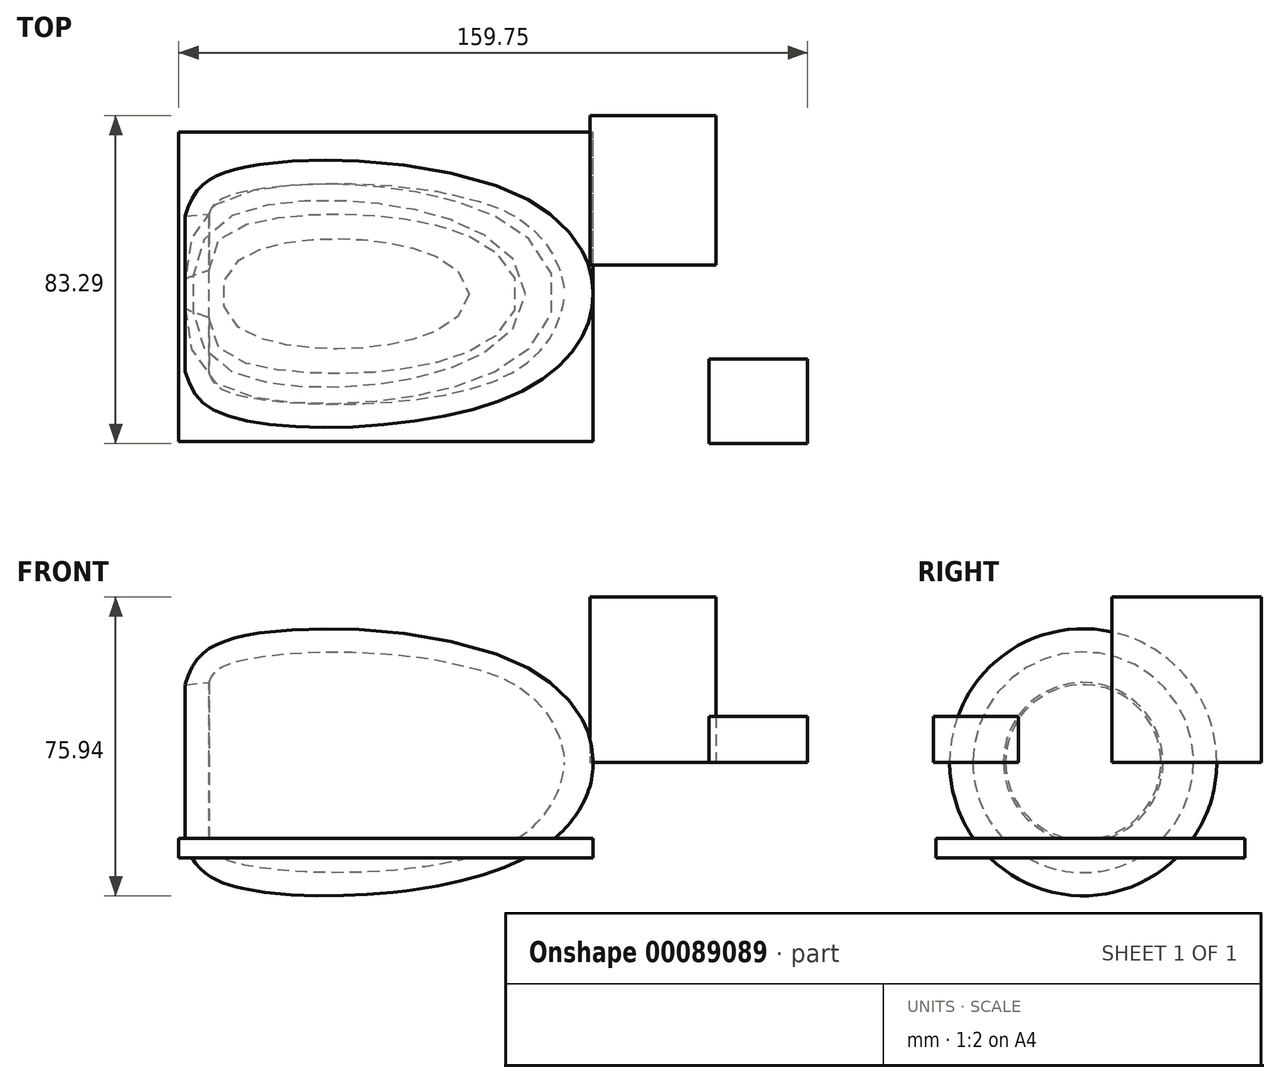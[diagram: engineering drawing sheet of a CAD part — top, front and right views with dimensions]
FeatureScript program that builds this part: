
annotation { "Feature Type Name" : "Feature", "Feature Type Description" : "" }
export const myFeature = defineFeature(function(context is Context, id is Id, definition is map)
    precondition{}
    {
        {
            var Q0;
            Q0=qCreatedBy(makeId("Top.planeOp"),FACE);
            var sketch = newSketch(context, id + "F0", { "sketchPlane" : qUnion([Q0])});
            skFitSpline(sketch, "E0", {"points": [v(0, 0) * mm, v(-17.7, -24.57) * mm, v(-92.32, -31.2) * mm, v(-103.63, -19.71) * mm], "startDerivative": vector(2.43, -78.93) * mm, "endDerivative": vector(-22.13, 76.46) * mm});
            skLineSegment(sketch, "E1", {"start": v(-103.63, -19.71) * mm, "end": v(-97.62, -20.26) * mm});
            skLineSegment(sketch, "E2", {"start": v(0, 0) * mm, "end": v(-7.26, 0) * mm});
            skFitSpline(sketch, "E3", {"points": [v(-97.62, -20.26) * mm, v(-91.53, -25.34) * mm, v(-20.71, -20.17) * mm, v(-7.26, 0) * mm], "startDerivative": vector(12.73, -36.05) * mm, "endDerivative": vector(2.5, 51.01) * mm});
            skSolve(sketch);
        }
        {
            var Q0;
            Q0=qCreatedBy(makeId("Top.planeOp"),FACE);
            var sketch = newSketch(context, id + "F1", { "sketchPlane" : qUnion([Q0])});
            skLineSegment(sketch, "E4", {"start": v(-123.98, 0) * mm, "end": v(-10.9, 0) * mm});
            skSolve(sketch);
        }
        {
            var Q0;
            Q0=makeQuery(id+"F0.imprint","IMPRINT",FACE,{"disambiguationData":[TD([[makeQuery(id+"F0.imprint","IMPRINT",EDGE,{"derivedFrom":sQuery(id+"F0.wireOp",EDGE,"E0")}),-1.0]])]});
            var Q1;
            Q1=sQuery(id+"F1.wireOp",EDGE,"E4");
            revolve(context, id + "F2", {"entities" : qUnion([Q0]), "axis" : qUnion([Q1]), "revolveType" : RevolveType.FULL});
        }
        {
            var Q0;
            Q0=qCreatedBy(makeId("Front.planeOp"),FACE);
            var sketch = newSketch(context, id + "F3", { "sketchPlane" : qUnion([Q0])});
            skLineSegment(sketch, "E5.bottom", {"start": v(-105.25, -19.35) * mm, "end": v(0, -19.35) * mm});
            skLineSegment(sketch, "E5.top", {"start": v(-105.25, -24.3) * mm, "end": v(0, -24.3) * mm});
            skLineSegment(sketch, "E5.left", {"start": v(-105.25, -19.35) * mm, "end": v(-105.25, -24.3) * mm});
            skLineSegment(sketch, "E5.right", {"start": v(0, -19.35) * mm, "end": v(0, -24.3) * mm});
            skSolve(sketch);
        }
        {
            var Q0;
            Q0=makeQuery(id+"F3.imprint","IMPRINT",FACE,{"disambiguationData":[TD([[makeQuery(id+"F3.imprint","IMPRINT",EDGE,{"derivedFrom":sQuery(id+"F3.wireOp",EDGE,"E5.bottom")}),-1.0]])]});
            extrude(context, id + "F4", {"entities" : qUnion([Q0]), "operationType" : NewBodyOperationType.ADD, "depth" : 37.48 * mm, "hasSecondDirection" : true, "secondDirectionOppositeDirection" : true, "secondDirectionDepth" : 41.05 * mm});
        }
        {
            var Q0;
            Q0=qCreatedBy(makeId("Top.planeOp"),FACE);
            var sketch = newSketch(context, id + "F5", { "sketchPlane" : qUnion([Q0])});
            skLineSegment(sketch, "E6.bottom", {"start": v(29.4, -16.52) * mm, "end": v(54.5, -16.52) * mm});
            skLineSegment(sketch, "E6.top", {"start": v(29.4, -38.02) * mm, "end": v(54.5, -38.02) * mm});
            skLineSegment(sketch, "E6.left", {"start": v(29.4, -16.52) * mm, "end": v(29.4, -38.02) * mm});
            skLineSegment(sketch, "E6.right", {"start": v(54.5, -16.52) * mm, "end": v(54.5, -38.02) * mm});
            skSolve(sketch);
        }
        {
            var Q0;
            Q0 = qSketchRegion(id + "F5", true);
            extrude(context, id + "F6", {"entities" : qUnion([Q0]), "depth" : 11.7 * mm});
        }
        {
            var Q0;
            Q0=qCreatedBy(makeId("Top.planeOp"),FACE);
            var sketch = newSketch(context, id + "F7", { "sketchPlane" : qUnion([Q0])});
            skLineSegment(sketch, "E7.bottom", {"start": v(-0.83, 45.27) * mm, "end": v(31.17, 45.27) * mm});
            skLineSegment(sketch, "E7.top", {"start": v(-0.83, 7.27) * mm, "end": v(31.17, 7.27) * mm});
            skLineSegment(sketch, "E7.left", {"start": v(-0.83, 45.27) * mm, "end": v(-0.83, 7.27) * mm});
            skLineSegment(sketch, "E7.right", {"start": v(31.17, 45.27) * mm, "end": v(31.17, 7.27) * mm});
            skSolve(sketch);
        }
        {
            var Q0;
            Q0 = qSketchRegion(id + "F7", true);
            extrude(context, id + "F8", {"entities" : qUnion([Q0]), "depth" : 42 * mm});
        }
    });
